# Revit family: KingswayGroup_AccssPnls_Anti-LigatureAccessPanel
name_source: partatom
category: Specialty Equipment
units: mm (PartAtom-declared; Revit-internal decimal feet)

## family parameters
Always vertical = Yes
Cut with Voids When Loaded = No
Part Type = Normal
Room Calculation Point = No
Round Connector Dimension = Use Diameter
Shared = No
Work Plane-Based = No

## types (1)
- KingswayGroup_AccssPnls_Anti-LigatureAccessPanel
    AssetType = Fixed
    BIMObjectName = KingswayGroup_AccessPanels_Anti-LigatureAccessPanel
    Category = Pr_30_59_36_01:Access panels
    Color = For full range of available finishes and colours, contact Kingsway Group
    Default Elevation = 0 mm  [stored 0 ft]
    Description = Access Panel 450 x 450 mm
    DoorMaterial = NBS_Concept
    DurationUnit = year
    Features = A highly secure Anti-Ligature Access Panel designed for ease of operation whilst minimising the ligature risk and protecting against self-harming. The secure steel panel allows for simple yet secure access to vital services whilst protecting against the risk of fire and physical product abuse.
    Finish = For full range of available finishes and colours, contact Kingsway Group
    IfcExportAs = IfcDoorType
    IfcExportType = USERDEFINED
    LockMaterial = NBS_Concept
    Manufacturer = Kingsway Group
    ManufacturerName = Kingsway Group
    ManufacturerURL = https://kingswaygroupglobal.com
    Material = Steel
    Model = KG362
    ModelNumber = KG362
    ModelReference = Anti-Ligature Access Panel
    Name = AccessPanels_Anti-LigatureAccessPanel_KG362_KingswayGroup
    NominalHeight = 508 mm
    NominalLength = 508 mm
    NominalWidth = 38 mm  [stored 0.124672 ft]
    ProductInformation = https://kingswaygroupglobal.com
    Size = 450 x 450 mm
    URL = https://kingswaygroupglobal.com
    Uniclass2015Code = Pr_30_59_36_01
    Uniclass2015Title = Access panels
    Uniclass2015Version = Products v1.36
    Version = 1
    WarrantyDescription = 5-Year Guarantee *For faulty manufacture and not for damage
    WarrantyDurationParts = 5
    WarrantyDurationUnit = year

note: [stored X ft] marks values corroborated as IEEE doubles in the binary element streams (Revit-internal decimal feet)

## geometry (parser evidence)
native form markers: Sweep x2
no freeform markers — native parametric forms only
